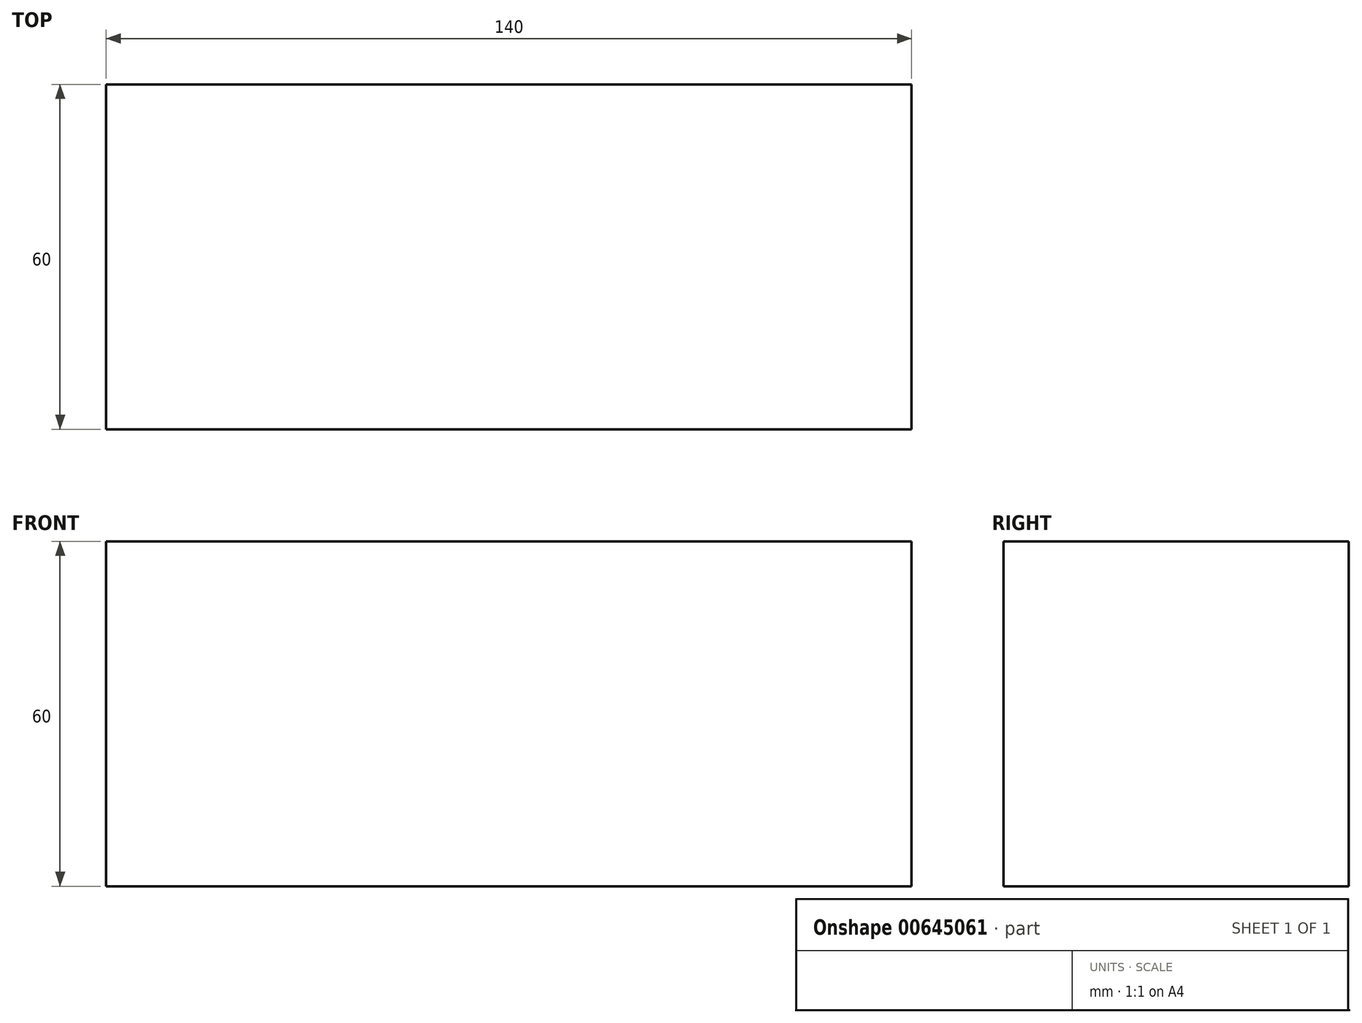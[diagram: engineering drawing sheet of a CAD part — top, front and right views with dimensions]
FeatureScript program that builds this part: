
annotation { "Feature Type Name" : "Feature", "Feature Type Description" : "" }
export const myFeature = defineFeature(function(context is Context, id is Id, definition is map)
    precondition{}
    {
        {
            var Q0;
            Q0=qCreatedBy(makeId("Top.planeOp"),FACE);
            var sketch = newSketch(context, id + "F0", { "sketchPlane" : qUnion([Q0])});
            skLineSegment(sketch, "E0.bottom", {"start": v(70, -30) * mm, "end": v(-70, -30) * mm});
            skLineSegment(sketch, "E0.top", {"start": v(70, 30) * mm, "end": v(-70, 30) * mm});
            skLineSegment(sketch, "E0.left", {"start": v(70, -30) * mm, "end": v(70, 30) * mm});
            skLineSegment(sketch, "E0.right", {"start": v(-70, -30) * mm, "end": v(-70, 30) * mm});
            skPoint(sketch, "E0.middle", {"position": v(0, 0) * mm});
            skSolve(sketch);
        }
        {
            var Q0;
            Q0 = qSketchRegion(id + "F0", true);
            extrude(context, id + "F1", {"entities" : qUnion([Q0]), "depth" : 60 * mm, "offsetDistance" : 25 * mm});
        }
        {
            var Q0;
            Q0=makeQuery(id+"F1.opExtrude","CAP_FACE",FACE,{"disambiguationData":[OSD([sQuery(id+"F0.wireOp",EDGE,"E0.bottom"),sQuery(id+"F0.wireOp",EDGE,"E0.top"),sQuery(id+"F0.wireOp",EDGE,"E0.left"),sQuery(id+"F0.wireOp",EDGE,"E0.right")])],"isStart":false});
            var sketch = newSketch(context, id + "F2", { "sketchPlane" : qUnion([Q0])});
            skCircle(sketch, "E1", {"center": v(40, 0) * mm, "radius": 10 * mm});
            skSolve(sketch);
        }
    });
